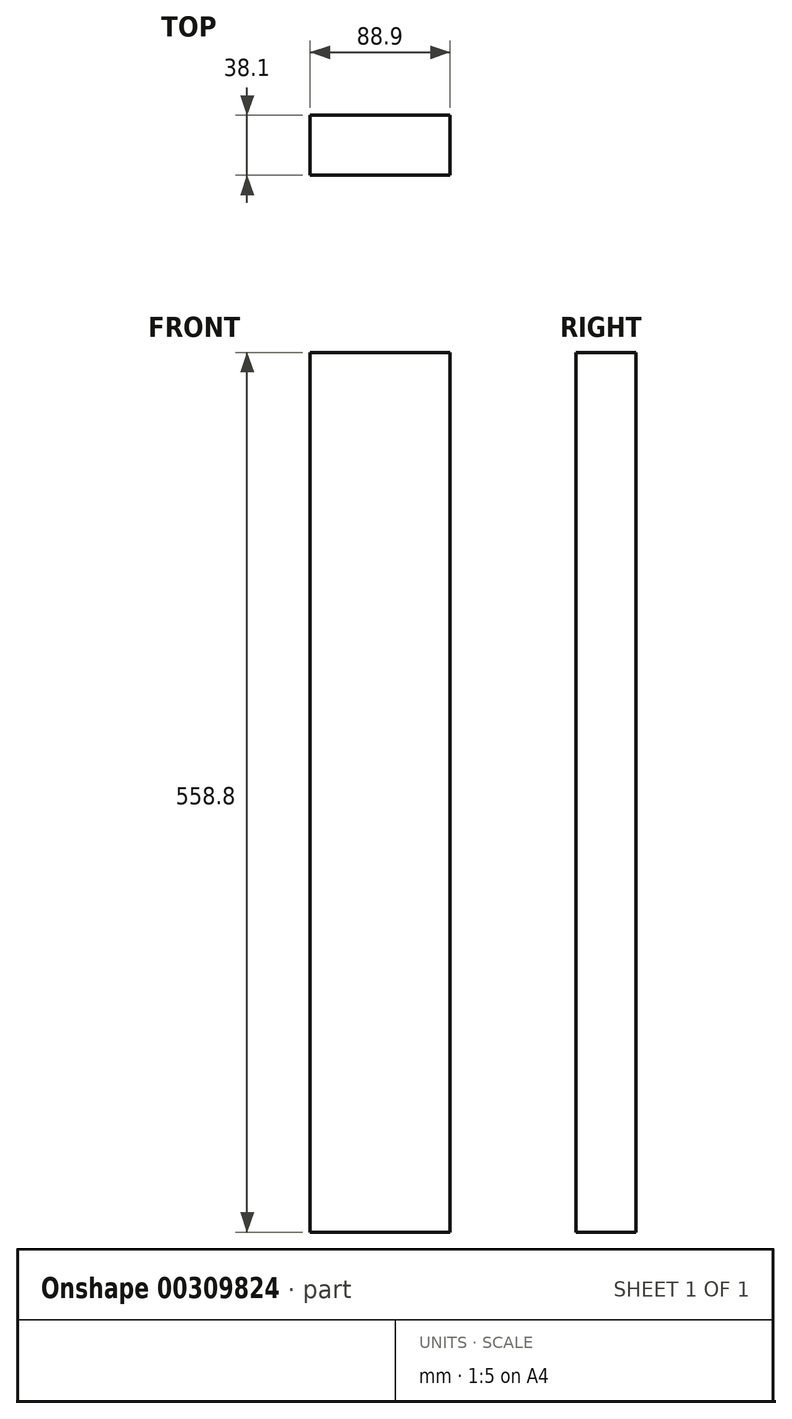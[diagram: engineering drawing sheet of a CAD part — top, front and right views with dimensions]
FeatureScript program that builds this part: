
annotation { "Feature Type Name" : "Feature", "Feature Type Description" : "" }
export const myFeature = defineFeature(function(context is Context, id is Id, definition is map)
    precondition{}
    {
        {
            var Q0;
            Q0=qCreatedBy(makeId("Front.planeOp"),FACE);
            var sketch = newSketch(context, id + "F0", { "sketchPlane" : qUnion([Q0])});
            skLineSegment(sketch, "E0.bottom", {"start": v(44.45, 279.4) * mm, "end": v(-44.45, 279.4) * mm});
            skLineSegment(sketch, "E0.top", {"start": v(44.45, -279.4) * mm, "end": v(-44.45, -279.4) * mm});
            skLineSegment(sketch, "E0.left", {"start": v(44.45, 279.4) * mm, "end": v(44.45, -279.4) * mm});
            skLineSegment(sketch, "E0.right", {"start": v(-44.45, 279.4) * mm, "end": v(-44.45, -279.4) * mm});
            skPoint(sketch, "E0.middle", {"position": v(0, 0) * mm});
            skSolve(sketch);
        }
        {
            var Q0;
            Q0=qSketchRegion(id+"F0",true);
            extrude(context, id + "F1", {"entities" : qUnion([Q0]), "depth" : 38.1 * mm});
        }
    });
